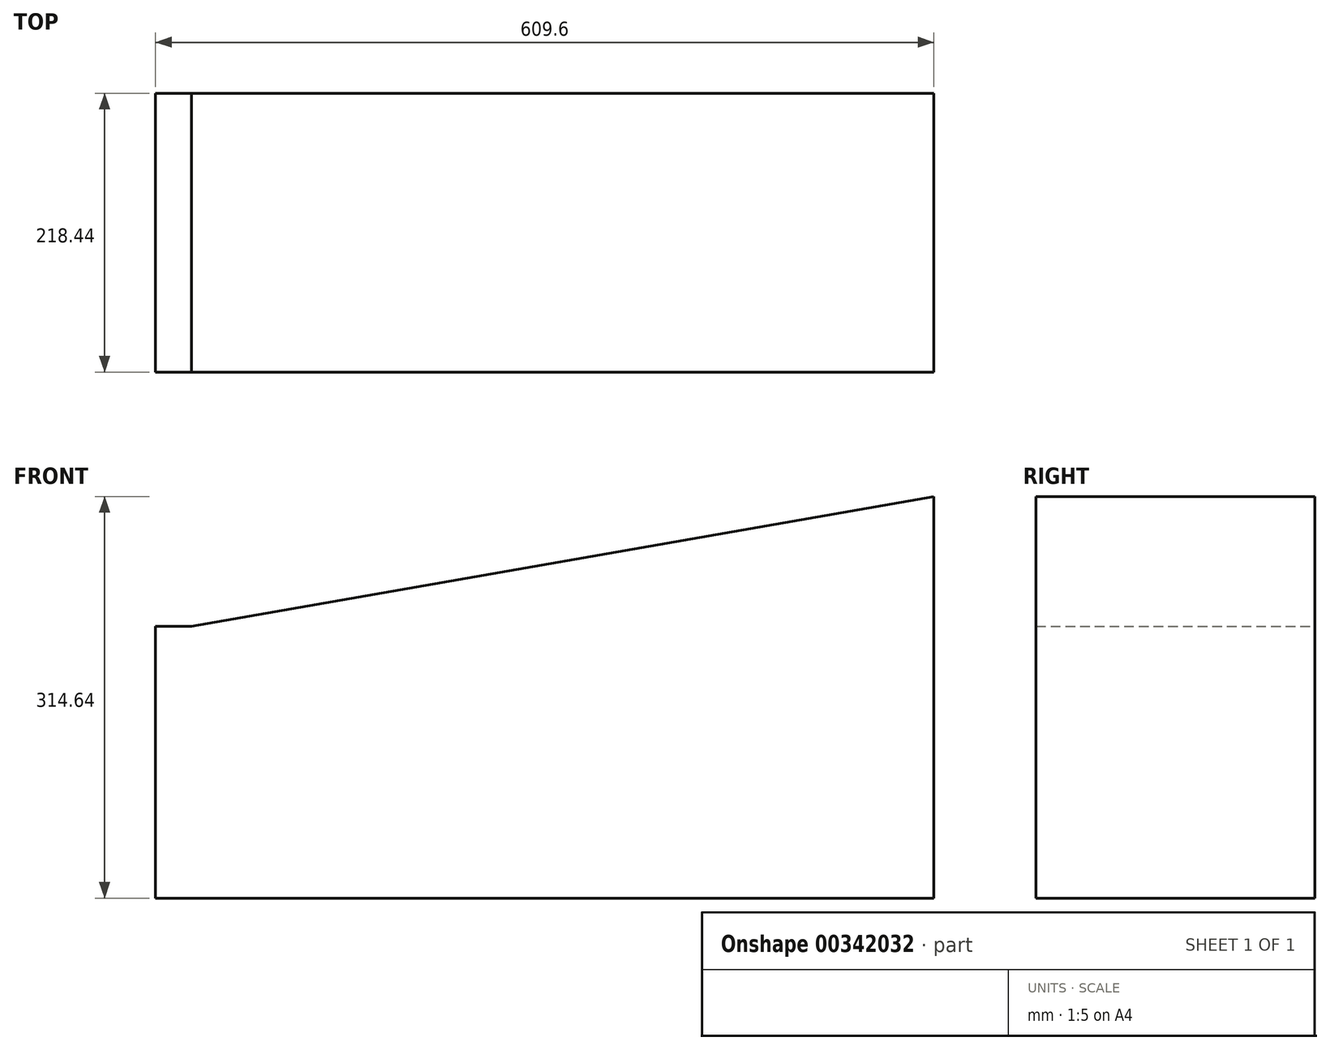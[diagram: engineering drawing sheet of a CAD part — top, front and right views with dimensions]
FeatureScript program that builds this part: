
annotation { "Feature Type Name" : "Feature", "Feature Type Description" : "" }
export const myFeature = defineFeature(function(context is Context, id is Id, definition is map)
    precondition{}
    {
        {
            var Q0;
            Q0=qCreatedBy(makeId("Front.planeOp"),FACE);
            var sketch = newSketch(context, id + "F0", { "sketchPlane" : qUnion([Q0])});
            skLineSegment(sketch, "E0.bottom", {"start": v(304.8, -106.52) * mm, "end": v(-304.8, -106.52) * mm});
            skLineSegment(sketch, "E0.top", {"start": v(304.8, 106.52) * mm, "end": v(-304.8, 106.52) * mm});
            skLineSegment(sketch, "E0.left", {"start": v(304.8, -106.52) * mm, "end": v(304.8, 106.52) * mm});
            skLineSegment(sketch, "E0.right", {"start": v(-304.8, -106.52) * mm, "end": v(-304.8, 106.52) * mm});
            skPoint(sketch, "E0.middle", {"position": v(0, 0) * mm});
            skLineSegment(sketch, "E1.bottom", {"start": v(304.8, -101.6) * mm, "end": v(-304.8, -101.6) * mm});
            skLineSegment(sketch, "E1.top", {"start": v(304.8, 101.6) * mm, "end": v(-304.8, 101.6) * mm});
            skLineSegment(sketch, "E1.left", {"start": v(304.8, -101.6) * mm, "end": v(304.8, 101.6) * mm});
            skLineSegment(sketch, "E1.right", {"start": v(-304.8, -101.6) * mm, "end": v(-304.8, 101.6) * mm});
            skLineSegment(sketch, "E2", {"start": v(-304.8, 101.6) * mm, "end": v(304.8, 208.12) * mm});
            skLineSegment(sketch, "E3", {"start": v(304.8, 208.12) * mm, "end": v(304.8, 101.6) * mm});
            skPoint(sketch, "E4", {"position": v(-304.8, 101.6) * mm});
            skPoint(sketch, "E5", {"position": v(-304.8, 106.52) * mm});
            skSolve(sketch);
        }
        {
            var Q0;
            Q0 = qSketchRegion(id + "F0", true);
            extrude(context, id + "F1", {"entities" : qUnion([Q0]), "depth" : 218.44 * mm});
        }
    });
